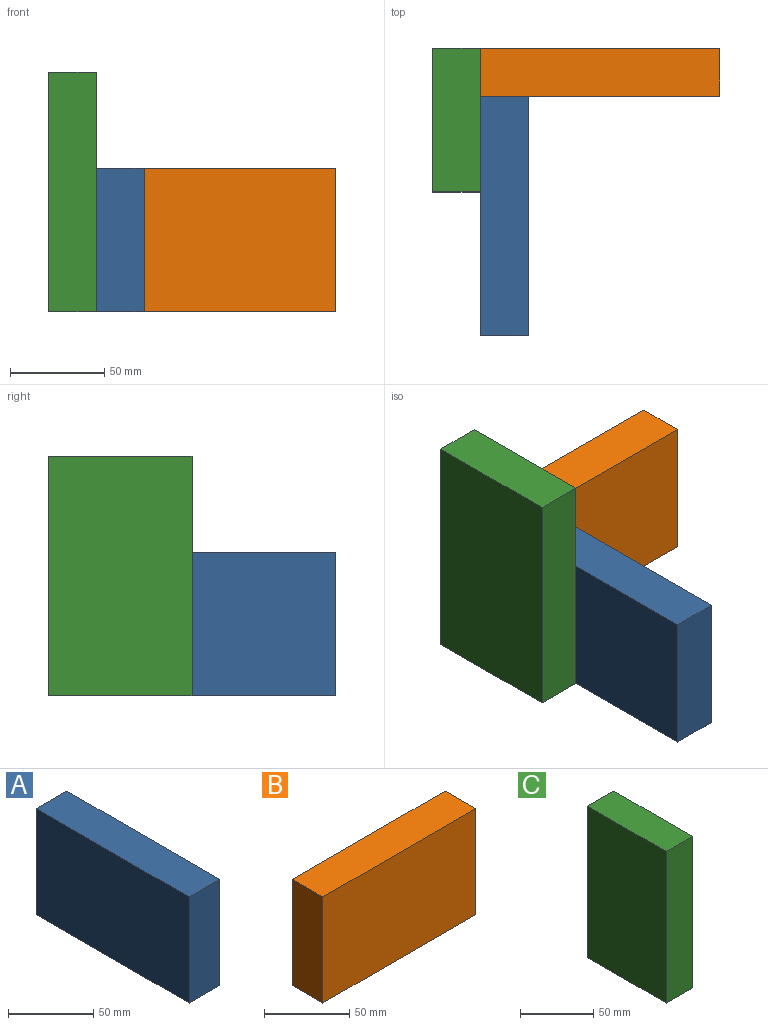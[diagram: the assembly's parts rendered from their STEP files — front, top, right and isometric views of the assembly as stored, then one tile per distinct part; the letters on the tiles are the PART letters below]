
ASSEMBLY  parts=3 mates=6
PART A: 6 faces, bbox 25.4x127x76.2 mm
  f0: plane 127x76.2mm, normal (1,0,0), area 9677.4mm2, adj f1,f3,f4,f5
  f1: plane 127x25.4mm, normal (0,0,1), area 3225.8mm2, adj f0,f2,f4,f5
  f2: plane 127x76.2mm, normal (-1,0,0), area 9677.4mm2, adj f1,f3,f4,f5
  f3: plane 127x25.4mm, normal (0,0,-1), area 3225.8mm2, adj f0,f2,f4,f5
  f4: plane 76.2x25.4mm, normal (0,-1,0), area 1935.5mm2, adj f0,f1,f2,f3
  f5: plane 76.2x25.4mm, normal (0,1,0), area 1935.5mm2, adj f0,f1,f2,f3
PART B: 6 faces, bbox 127x25.4x76.2 mm
  f0: plane 127x25.4mm, normal (0,0,1), area 3225.8mm2, adj f1,f3,f4,f5
  f1: plane 127x76.2mm, normal (0,-1,0), area 9677.4mm2, adj f0,f2,f4,f5
  f2: plane 127x25.4mm, normal (0,0,-1), area 3225.8mm2, adj f1,f3,f4,f5
  f3: plane 127x76.2mm, normal (0,1,0), area 9677.4mm2, adj f0,f2,f4,f5
  f4: plane 76.2x25.4mm, normal (1,0,0), area 1935.5mm2, adj f0,f1,f2,f3
  f5: plane 76.2x25.4mm, normal (-1,0,0), area 1935.5mm2, adj f0,f1,f2,f3
PART C: 6 faces, bbox 25.4x76.2x127 mm
  f0: plane 127x76.2mm, normal (1,0,0), area 9677.4mm2, adj f1,f3,f4,f5
  f1: plane 127x25.4mm, normal (0,1,0), area 3225.8mm2, adj f0,f2,f4,f5
  f2: plane 127x76.2mm, normal (-1,0,0), area 9677.4mm2, adj f1,f3,f4,f5
  f3: plane 127x25.4mm, normal (0,-1,0), area 3225.8mm2, adj f0,f2,f4,f5
  f4: plane 76.2x25.4mm, normal (0,0,1), area 1935.5mm2, adj f0,f1,f2,f3
  f5: plane 76.2x25.4mm, normal (0,0,-1), area 1935.5mm2, adj f0,f1,f2,f3
PLACE A t=(-193.58,43.82,92.55)mm
PLACE B t=(-218.98,43.82,92.55)mm
PLACE C t=(-218.98,-6.98,92.55)mm
MATE planar A.f2 <-> C.f0  axis (-1,0,0) through (-218.98,-19.68,130.65)mm
MATE planar A.f3 <-> C.f5  axis (0,0,-1) through (-206.28,-19.68,92.55)mm
MATE planar B.f3 <-> C.f1  axis (0,1,0) through (-155.48,69.22,130.65)mm
MATE planar B.f5 <-> C.f0  axis (-1,0,0) through (-218.98,69.22,130.65)mm
MATE planar B.f2 <-> C.f5  axis (0,0,-1) through (-155.48,56.52,92.55)mm
MATE planar A.f5 <-> B.f1  axis (0,1,0) through (-206.28,43.82,130.65)mm
